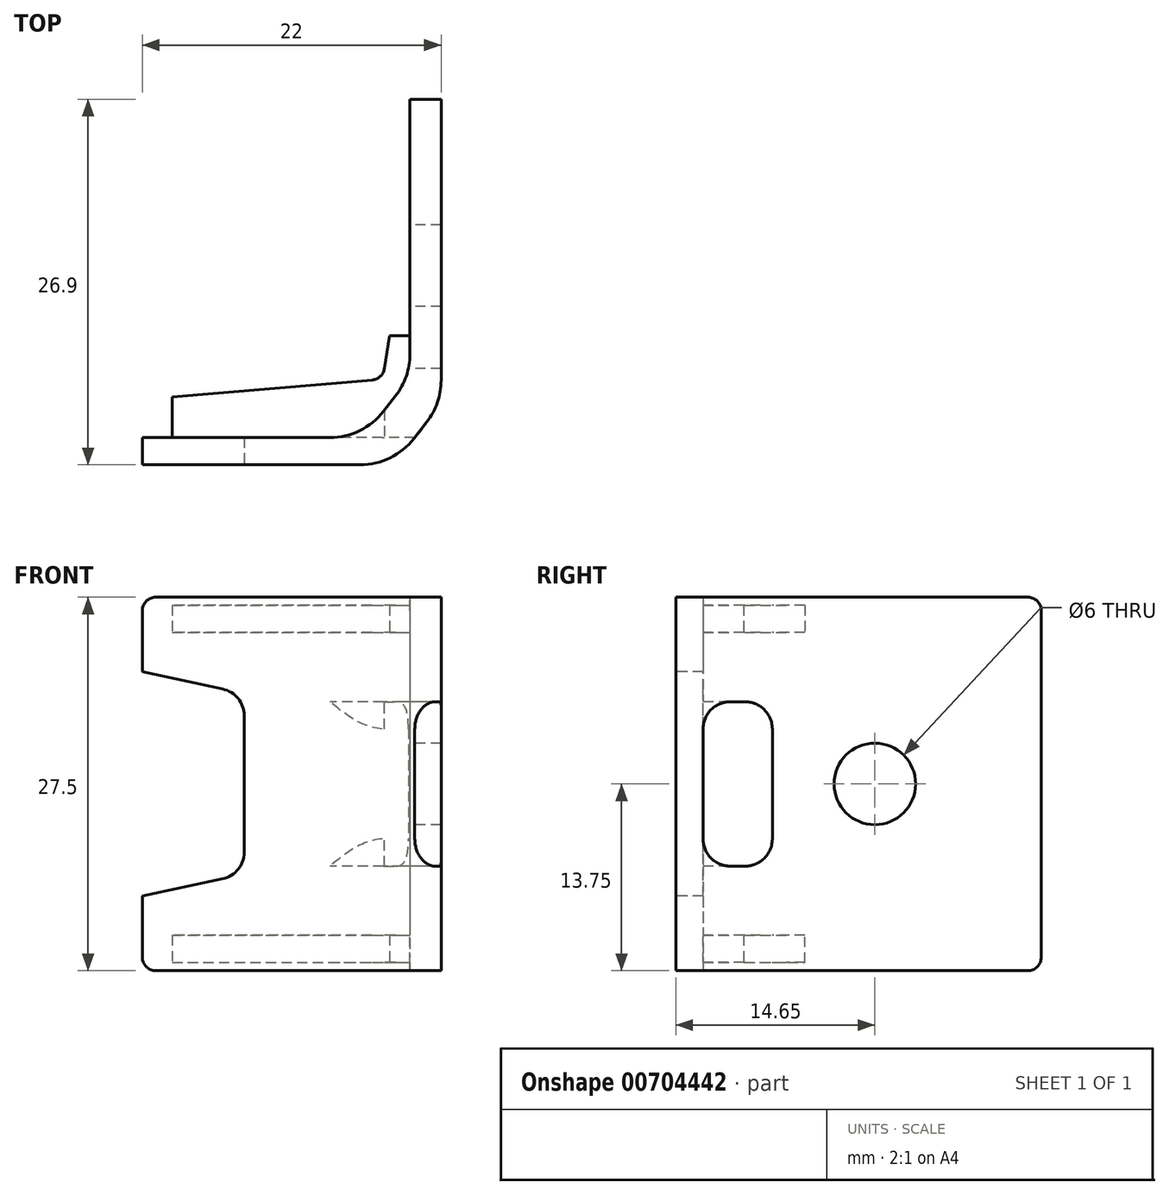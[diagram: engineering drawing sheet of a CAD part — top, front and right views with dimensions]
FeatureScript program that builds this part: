
annotation { "Feature Type Name" : "Feature", "Feature Type Description" : "" }
export const myFeature = defineFeature(function(context is Context, id is Id, definition is map)
    precondition{}
    {
        {
            var Q0;
            Q0=qCreatedBy(makeId("Top.planeOp"),FACE);
            var sketch = newSketch(context, id + "F0", { "sketchPlane" : qUnion([Q0])});
            skLineSegment(sketch, "E0", {"start": v(0, 0) * mm, "end": v(16.05, 0) * mm});
            skLineSegment(sketch, "E1", {"start": v(22, 6.22) * mm, "end": v(22, 26.9) * mm});
            skLineSegment(sketch, "E2", {"start": v(22, 26.9) * mm, "end": v(19.7, 26.9) * mm});
            skLineSegment(sketch, "E3", {"start": v(19.7, 26.9) * mm, "end": v(19.7, 8.14) * mm});
            skLineSegment(sketch, "E4", {"start": v(13.8, 2) * mm, "end": v(0, 2) * mm});
            skLineSegment(sketch, "E5", {"start": v(0, 2) * mm, "end": v(0, 0) * mm});
            skLineSegment(sketch, "E6", {"start": v(20.95, 3.15) * mm, "end": v(20, 1.93) * mm});
            skLineSegment(sketch, "E7", {"start": v(18.65, 5.08) * mm, "end": v(17.76, 3.93) * mm});
            skPoint(sketch, "E8.visualSharp", {"position": v(22, 4.5) * mm});
            skArc(sketch, "E8.filletArc", {"start": v(20.95, 3.15) * mm, "mid": v(21.73, 4.6) * mm, "end": v(22, 6.22) * mm});
            skPoint(sketch, "E9.visualSharp", {"position": v(18.5, 0) * mm});
            skArc(sketch, "E9.filletArc", {"start": v(16.05, 0) * mm, "mid": v(18.25, 0.5) * mm, "end": v(20, 1.93) * mm});
            skPoint(sketch, "E10.visualSharp", {"position": v(16.25, 2) * mm});
            skArc(sketch, "E10.filletArc", {"start": v(13.8, 2) * mm, "mid": v(16, 2.5) * mm, "end": v(17.76, 3.93) * mm});
            skPoint(sketch, "E11.visualSharp", {"position": v(19.7, 6.43) * mm});
            skArc(sketch, "E11.filletArc", {"start": v(18.65, 5.08) * mm, "mid": v(19.43, 6.52) * mm, "end": v(19.7, 8.14) * mm});
            skSolve(sketch);
        }
        {
            var Q0;
            Q0=makeQuery(id+"F0.imprint","IMPRINT",FACE,{"disambiguationData":[TD([[makeQuery(id+"F0.imprint","IMPRINT",EDGE,{"derivedFrom":sQuery(id+"F0.wireOp",EDGE,"E0")}),1.0]])]});
            extrude(context, id + "F1", {"entities" : qUnion([Q0]), "depth" : 27.5 * mm, "offsetDistance" : 25 * mm});
        }
        {
            var Q0;
            Q0=makeQuery(id+"F1.opExtrude","SWEPT_FACE",FACE,{"disambiguationData":[OSD([sQuery(id+"F0.wireOp",EDGE,"E3")])]});
            var sketch = newSketch(context, id + "F2", { "sketchPlane" : qUnion([Q0])});
            skLineSegment(sketch, "E12.bottom", {"start": v(-7.1, 19.8) * mm, "end": v(-2, 19.8) * mm});
            skLineSegment(sketch, "E12.top", {"start": v(-7.1, 7.7) * mm, "end": v(-2, 7.7) * mm});
            skLineSegment(sketch, "E12.left", {"start": v(-7.1, 19.8) * mm, "end": v(-7.1, 7.7) * mm});
            skLineSegment(sketch, "E12.right", {"start": v(-2, 19.8) * mm, "end": v(-2, 7.7) * mm});
            skCircle(sketch, "E13", {"center": v(-14.65, 13.75) * mm, "radius": 3 * mm});
            skPoint(sketch, "E13.centerSnap0", {"position": v(-26.9, 13.75) * mm});
            skSolve(sketch);
        }
        {
            var Q0;
            Q0 = qSketchRegion(id + "F2", true);
            extrude(context, id + "F3", {"entities" : qUnion([Q0]), "operationType" : NewBodyOperationType.REMOVE, "oppositeDirection" : true, "depth" : 25 * mm, "offsetDistance" : 25 * mm, "symmetric" : true});
        }
        {
            var Q0;
            Q0=makeQuery(id+"F1.opExtrude","SWEPT_FACE",FACE,{"disambiguationData":[OSD([sQuery(id+"F0.wireOp",EDGE,"E3")])]});
            var sketch = newSketch(context, id + "F4", { "sketchPlane" : qUnion([Q0])});
            skLineSegment(sketch, "E14.bottom", {"start": v(-9.5, 26.9) * mm, "end": v(-2, 26.9) * mm});
            skLineSegment(sketch, "E14.top", {"start": v(-9.5, 24.9) * mm, "end": v(-2, 24.9) * mm});
            skLineSegment(sketch, "E14.left", {"start": v(-9.5, 26.9) * mm, "end": v(-9.5, 24.9) * mm});
            skLineSegment(sketch, "E14.right", {"start": v(-2, 26.9) * mm, "end": v(-2, 24.9) * mm});
            skLineSegment(sketch, "E15", {"start": v(-26.9, 13.75) * mm, "end": v(0, 13.75) * mm, "construction": true});
            skLineSegment(sketch, "E16.MirrorCS", {"start": v(-9.5, 0.6) * mm, "end": v(-9.5, 2.6) * mm});
            skLineSegment(sketch, "E17.MirrorCS", {"start": v(-9.5, 0.6) * mm, "end": v(-2, 0.6) * mm});
            skLineSegment(sketch, "E18.MirrorCS", {"start": v(-9.5, 2.6) * mm, "end": v(-2, 2.6) * mm});
            skLineSegment(sketch, "E19.MirrorCS", {"start": v(-2, 0.6) * mm, "end": v(-2, 2.6) * mm});
            skSolve(sketch);
        }
        {
            var Q0;
            Q0 = qSketchRegion(id + "F4", true);
            extrude(context, id + "F5", {"entities" : qUnion([Q0]), "operationType" : NewBodyOperationType.ADD, "depth" : 17.5 * mm, "offsetDistance" : 25 * mm});
        }
        {
            var Q0;
            Q0=makeQuery(id+"F5.opExtrude","SWEPT_FACE",FACE,{"disambiguationData":[OSD([sQuery(id+"F4.wireOp",EDGE,"E17.MirrorCS")])]});
            var sketch = newSketch(context, id + "F6", { "sketchPlane" : qUnion([Q0])});
            skLineSegment(sketch, "E20", {"start": v(2.2, -5) * mm, "end": v(17.7, -6.3) * mm});
            skLineSegment(sketch, "E21", {"start": v(17.7, -6.3) * mm, "end": v(18.2, -9.5) * mm});
            skLineSegment(sketch, "E22", {"start": v(18.2, -9.5) * mm, "end": v(2.2, -9.5) * mm});
            skLineSegment(sketch, "E23", {"start": v(2.2, -9.5) * mm, "end": v(2.2, -5) * mm});
            skSolve(sketch);
        }
        {
            var Q0;
            Q0 = qSketchRegion(id + "F6", true);
            extrude(context, id + "F7", {"entities" : qUnion([Q0]), "operationType" : NewBodyOperationType.REMOVE, "endBound" : BoundingType.THROUGH_ALL, "oppositeDirection" : true, "depth" : 25 * mm, "offsetDistance" : 25 * mm});
        }
        {
            var Q0;
            {var subQ0=sQuery(id+"F4.wireOp",EDGE,"E17.MirrorCS");var subQ1=sQuery(id+"F6.wireOp",EDGE,"E20");Q0=makeQuery(id+"F7.boolean.opBoolean","COPY",EDGE,{"disambiguationData":[topologyDisambiguationEdgeConnected([makeQuery(id+"F5.opExtrude","CAP_FACE",FACE,{"disambiguationData":[OSD([sQuery(id+"F4.wireOp",EDGE,"E16.MirrorCS"),subQ0,sQuery(id+"F4.wireOp",EDGE,"E18.MirrorCS"),sQuery(id+"F4.wireOp",EDGE,"E19.MirrorCS")])],"isStart":false})])],"derivedFrom":makeQuery(id+"F7.opExtrude","SWEPT_EDGE",EDGE,{"disambiguationData":[OSD([subQ0,subQ1,sQuery(id+"F6.wireOp",EDGE,"E23")])]})});}
            var Q1;
            {var subQ0=sQuery(id+"F6.wireOp",EDGE,"E20");Q1=makeQuery(id+"F7.boolean.opBoolean","COPY",EDGE,{"disambiguationData":[topologyDisambiguationEdgeConnected([makeQuery(id+"F5.opExtrude","CAP_FACE",FACE,{"disambiguationData":[OSD([sQuery(id+"F4.wireOp",EDGE,"E14.bottom"),sQuery(id+"F4.wireOp",EDGE,"E14.top"),sQuery(id+"F4.wireOp",EDGE,"E14.left"),sQuery(id+"F4.wireOp",EDGE,"E14.right")])],"isStart":false})])],"derivedFrom":makeQuery(id+"F7.opExtrude","SWEPT_EDGE",EDGE,{"disambiguationData":[OSD([sQuery(id+"F4.wireOp",EDGE,"E17.MirrorCS"),subQ0,sQuery(id+"F6.wireOp",EDGE,"E23")])]})});}
            var Q2;
            Q2=makeQuery(id+"F1.opExtrude","CAP_EDGE",EDGE,{"disambiguationData":[OSD([sQuery(id+"F0.wireOp",EDGE,"E5")])],"isStart":true});
            var Q3;
            Q3=makeQuery(id+"F1.opExtrude","CAP_EDGE",EDGE,{"disambiguationData":[OSD([sQuery(id+"F0.wireOp",EDGE,"E5")])],"isStart":false});
            var Q4;
            Q4=makeQuery(id+"F1.opExtrude","CAP_EDGE",EDGE,{"disambiguationData":[OSD([sQuery(id+"F0.wireOp",EDGE,"E2")])],"isStart":true});
            var Q5;
            Q5=makeQuery(id+"F1.opExtrude","CAP_EDGE",EDGE,{"disambiguationData":[OSD([sQuery(id+"F0.wireOp",EDGE,"E2")])],"isStart":false});
            var Q6;
            {var subQ0=sQuery(id+"F6.wireOp",EDGE,"E20");var subQ1=sQuery(id+"F6.wireOp",EDGE,"E21");Q6=makeQuery(id+"F7.boolean.opBoolean","COPY",EDGE,{"disambiguationData":[TD([makeQuery(id+"F5.opExtrude","SWEPT_FACE",FACE,{"disambiguationData":[OSD([sQuery(id+"F4.wireOp",EDGE,"E17.MirrorCS")])]})])],"derivedFrom":makeQuery(id+"F7.opExtrude","SWEPT_EDGE",EDGE,{"disambiguationData":[OSD([subQ0,subQ1])]})});}
            var Q7;
            {var subQ0=sQuery(id+"F6.wireOp",EDGE,"E20");var subQ1=sQuery(id+"F6.wireOp",EDGE,"E21");Q7=makeQuery(id+"F7.boolean.opBoolean","COPY",EDGE,{"disambiguationData":[TD([makeQuery(id+"F5.opExtrude","SWEPT_FACE",FACE,{"disambiguationData":[OSD([sQuery(id+"F4.wireOp",EDGE,"E14.bottom")])]})])],"derivedFrom":makeQuery(id+"F7.opExtrude","SWEPT_EDGE",EDGE,{"disambiguationData":[OSD([subQ0,subQ1])]})});}
            fillet(context, id + "F8", {"entities" : qUnion([Q0, Q1, Q2, Q3, Q4, Q5, Q6, Q7]), "radius" : 1 * mm, "tangentPropagation" : true, "allowEdgeOverflow" : false});
        }
        {
            var Q0;
            Q0=makeQuery(id+"F3.boolean.opBoolean","COPY",EDGE,{"derivedFrom":makeQuery(id+"F3.opExtrude","SWEPT_EDGE",EDGE,{"disambiguationData":[OSD([sQuery(id+"F2.wireOp",EDGE,"E12.bottom"),sQuery(id+"F2.wireOp",EDGE,"E12.right")])]})});
            var Q1;
            Q1=makeQuery(id+"F3.boolean.opBoolean","COPY",EDGE,{"derivedFrom":makeQuery(id+"F3.opExtrude","SWEPT_EDGE",EDGE,{"disambiguationData":[OSD([sQuery(id+"F2.wireOp",EDGE,"E12.bottom"),sQuery(id+"F2.wireOp",EDGE,"E12.left")])]})});
            var Q2;
            Q2=makeQuery(id+"F3.boolean.opBoolean","COPY",EDGE,{"derivedFrom":makeQuery(id+"F3.opExtrude","SWEPT_EDGE",EDGE,{"disambiguationData":[OSD([sQuery(id+"F2.wireOp",EDGE,"E12.top"),sQuery(id+"F2.wireOp",EDGE,"E12.right")])]})});
            var Q3;
            Q3=makeQuery(id+"F3.boolean.opBoolean","COPY",EDGE,{"derivedFrom":makeQuery(id+"F3.opExtrude","SWEPT_EDGE",EDGE,{"disambiguationData":[OSD([sQuery(id+"F2.wireOp",EDGE,"E12.top"),sQuery(id+"F2.wireOp",EDGE,"E12.left")])]})});
            fillet(context, id + "F9", {"entities" : qUnion([Q0, Q1, Q2, Q3]), "radius" : 2 * mm, "tangentPropagation" : true, "allowEdgeOverflow" : false});
        }
        {
            var Q0;
            Q0=makeQuery(id+"F1.opExtrude","SWEPT_FACE",FACE,{"disambiguationData":[OSD([sQuery(id+"F0.wireOp",EDGE,"E0")])]});
            var sketch = newSketch(context, id + "F10", { "sketchPlane" : qUnion([Q0])});
            skLineSegment(sketch, "E24", {"start": v(0, 5.5) * mm, "end": v(7.5, 7.1) * mm});
            skLineSegment(sketch, "E25", {"start": v(7.5, 7.1) * mm, "end": v(7.5, 20.4) * mm});
            skLineSegment(sketch, "E26", {"start": v(7.5, 20.4) * mm, "end": v(0, 22) * mm});
            skLineSegment(sketch, "E27", {"start": v(0, 13.75) * mm, "end": v(22, 13.75) * mm, "construction": true});
            skSolve(sketch);
        }
        {
            var Q0;
            {var subQ0=sQuery(id+"F10.wireOp",EDGE,"E24");Q0=makeQuery(id+"F10.imprint","IMPRINT",FACE,{"disambiguationData":[TD([[makeQuery(id+"F10.imprint","IMPRINT",EDGE,{"derivedFrom":subQ0}),1.0]])]});}
            extrude(context, id + "F11", {"entities" : qUnion([Q0]), "operationType" : NewBodyOperationType.REMOVE, "endBound" : BoundingType.THROUGH_ALL, "oppositeDirection" : true, "depth" : 25 * mm, "offsetDistance" : 25 * mm});
        }
        {
            var Q0;
            Q0=makeQuery(id+"F11.boolean.opBoolean","COPY",EDGE,{"derivedFrom":makeQuery(id+"F11.opExtrude","SWEPT_EDGE",EDGE,{"disambiguationData":[OSD([sQuery(id+"F0.wireOp",EDGE,"E0"),sQuery(id+"F0.wireOp",EDGE,"E5"),sQuery(id+"F10.wireOp",EDGE,"E24")])]})});
            var Q1;
            Q1=makeQuery(id+"F11.boolean.opBoolean","COPY",EDGE,{"derivedFrom":makeQuery(id+"F11.opExtrude","SWEPT_EDGE",EDGE,{"disambiguationData":[OSD([sQuery(id+"F0.wireOp",EDGE,"E0"),sQuery(id+"F0.wireOp",EDGE,"E5"),sQuery(id+"F10.wireOp",EDGE,"E26")])]})});
            var Q2;
            Q2=makeQuery(id+"F11.boolean.opBoolean","COPY",EDGE,{"derivedFrom":makeQuery(id+"F11.opExtrude","SWEPT_EDGE",EDGE,{"disambiguationData":[OSD([sQuery(id+"F10.wireOp",EDGE,"E25"),sQuery(id+"F10.wireOp",EDGE,"E26")])]})});
            var Q3;
            Q3=makeQuery(id+"F11.boolean.opBoolean","COPY",EDGE,{"derivedFrom":makeQuery(id+"F11.opExtrude","SWEPT_EDGE",EDGE,{"disambiguationData":[OSD([sQuery(id+"F10.wireOp",EDGE,"E24"),sQuery(id+"F10.wireOp",EDGE,"E25")])]})});
            fillet(context, id + "F12", {"entities" : qUnion([Q0, Q1, Q2, Q3]), "radius" : 2 * mm, "tangentPropagation" : true, "allowEdgeOverflow" : false});
        }
    });
